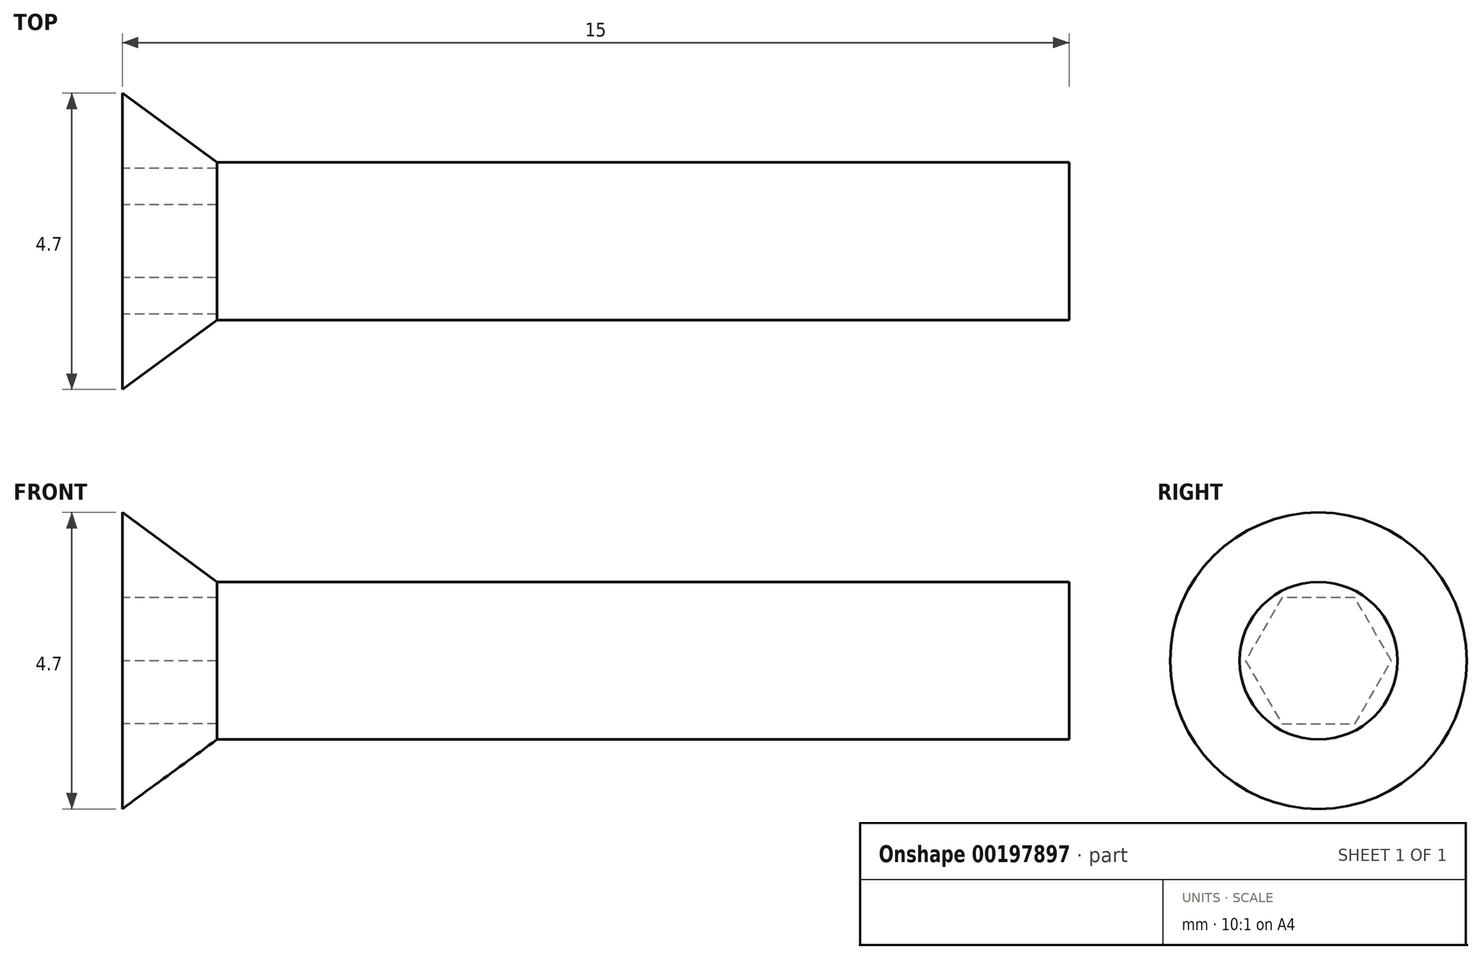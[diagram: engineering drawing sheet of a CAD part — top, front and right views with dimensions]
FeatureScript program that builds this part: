
annotation { "Feature Type Name" : "Feature", "Feature Type Description" : "" }
export const myFeature = defineFeature(function(context is Context, id is Id, definition is map)
    precondition{}
    {
        {
            var Q0;
            Q0=qCreatedBy(makeId("Front.planeOp"),FACE);
            var sketch = newSketch(context, id + "F0", { "sketchPlane" : qUnion([Q0])});
            skLineSegment(sketch, "E0", {"start": v(0, 0) * mm, "end": v(0, 2.35) * mm});
            skLineSegment(sketch, "E1", {"start": v(0, 2.35) * mm, "end": v(1.5, 1.25) * mm});
            skLineSegment(sketch, "E2", {"start": v(1.5, 1.25) * mm, "end": v(15, 1.25) * mm});
            skLineSegment(sketch, "E3", {"start": v(15, 1.25) * mm, "end": v(15, 0) * mm});
            skLineSegment(sketch, "E4", {"start": v(15, 0) * mm, "end": v(0, 0) * mm});
            skSolve(sketch);
        }
        {
            var Q0;
            Q0=makeQuery(id+"F0.imprint","IMPRINT",FACE,{"disambiguationData":[TD([[makeQuery(id+"F0.imprint","IMPRINT",EDGE,{"derivedFrom":sQuery(id+"F0.wireOp",EDGE,"E0")}),-1.0]])]});
            var Q1;
            Q1=sQuery(id+"F0.wireOp",EDGE,"E4");
            revolve(context, id + "F1", {"entities" : qUnion([Q0]), "axis" : qUnion([Q1]), "revolveType" : RevolveType.FULL});
        }
        {
            var Q0;
            Q0=makeQuery(id+"F1.opRevolve","SWEPT_FACE",FACE,{"disambiguationData":[OSD([sQuery(id+"F0.wireOp",EDGE,"E0")])]});
            var sketch = newSketch(context, id + "F2", { "sketchPlane" : qUnion([Q0])});
            skCircle(sketch, "E5.cCircle", {"center": v(0, 0) * mm, "radius": 1.15 * mm, "construction": true});
            skLineSegment(sketch, "E5.0", {"start": v(1.15, 0) * mm, "end": v(0.58, -1) * mm});
            skLineSegment(sketch, "E5.1", {"start": v(0.58, -1) * mm, "end": v(-0.58, -1) * mm});
            skLineSegment(sketch, "E5.2", {"start": v(-0.58, -1) * mm, "end": v(-1.15, 0) * mm});
            skLineSegment(sketch, "E5.3", {"start": v(-1.15, 0) * mm, "end": v(-0.58, 1) * mm});
            skLineSegment(sketch, "E5.4", {"start": v(-0.58, 1) * mm, "end": v(0.58, 1) * mm});
            skLineSegment(sketch, "E5.5", {"start": v(0.58, 1) * mm, "end": v(1.15, 0) * mm});
            skSolve(sketch);
        }
        {
            var Q0;
            Q0=makeQuery(id+"F2.imprint","IMPRINT",FACE,{"disambiguationData":[TD([[makeQuery(id+"F2.imprint","IMPRINT",EDGE,{"derivedFrom":sQuery(id+"F2.wireOp",EDGE,"E5.0")}),-1.0]])]});
            extrude(context, id + "F3", {"entities" : qUnion([Q0]), "operationType" : NewBodyOperationType.REMOVE, "oppositeDirection" : true, "depth" : 1.5 * mm});
        }
    });
